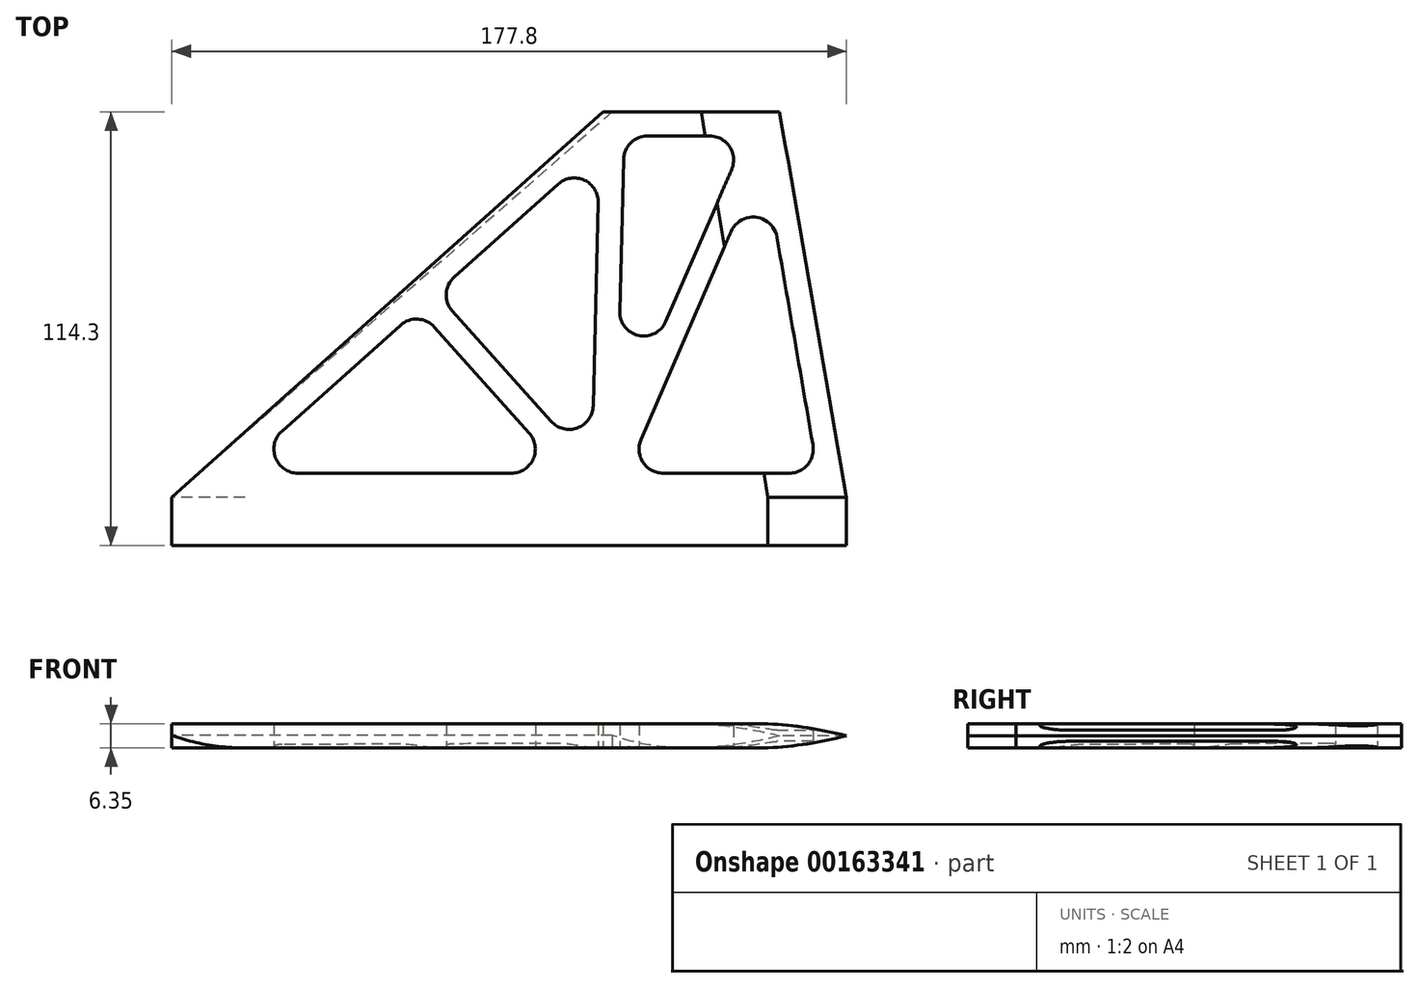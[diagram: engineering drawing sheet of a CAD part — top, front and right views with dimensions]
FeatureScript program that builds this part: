
annotation { "Feature Type Name" : "Feature", "Feature Type Description" : "" }
export const myFeature = defineFeature(function(context is Context, id is Id, definition is map)
    precondition{}
    {
        {
            var Q0;
            Q0=qCreatedBy(makeId("Top.planeOp"),FACE);
            var sketch = newSketch(context, id + "F0", { "sketchPlane" : qUnion([Q0])});
            skLineSegment(sketch, "E0", {"start": v(0, 0) * mm, "end": v(177.8, 0) * mm});
            skLineSegment(sketch, "E1", {"start": v(0, 0) * mm, "end": v(113.6, 101.6) * mm});
            skLineSegment(sketch, "E2", {"start": v(113.6, 101.6) * mm, "end": v(160.17, 101.6) * mm});
            skLineSegment(sketch, "E3", {"start": v(160.17, 101.6) * mm, "end": v(177.8, 0) * mm});
            skLineSegment(sketch, "E4.0", {"start": v(33.25, 6.35) * mm, "end": v(89.45, 6.35) * mm});
            skLineSegment(sketch, "E4.1", {"start": v(29.02, 17.43) * mm, "end": v(60.24, 45.36) * mm});
            skLineSegment(sketch, "E4.2", {"start": v(125.38, 95.25) * mm, "end": v(141.7, 95.25) * mm});
            skLineSegment(sketch, "E4.3", {"start": v(159.45, 68.6) * mm, "end": v(168.96, 13.79) * mm});
            skLineSegment(sketch, "E5.0", {"start": v(99.95, 20.02) * mm, "end": v(73.94, 49.1) * mm});
            skLineSegment(sketch, "E6.0", {"start": v(94.19, 16.93) * mm, "end": v(69.2, 44.86) * mm});
            skLineSegment(sketch, "E7.0", {"start": v(116.93, 6.27) * mm, "end": v(116.93, 6.35) * mm});
            skLineSegment(sketch, "E8.0", {"start": v(111.03, 24.09) * mm, "end": v(112.4, 77.65) * mm});
            skLineSegment(sketch, "E9.0", {"start": v(123.64, 15.22) * mm, "end": v(147.37, 70.03) * mm});
            skLineSegment(sketch, "E10.trimOffspring", {"start": v(118.02, 49.02) * mm, "end": v(119.04, 89.06) * mm});
            skLineSegment(sketch, "E11.trimOffspring", {"start": v(130.2, 46.34) * mm, "end": v(147.52, 86.38) * mm});
            skLineSegment(sketch, "E12.trimOffspring", {"start": v(129.47, 6.35) * mm, "end": v(162.7, 6.35) * mm});
            skLineSegment(sketch, "E13.trimOffspring", {"start": v(74.44, 58.06) * mm, "end": v(101.81, 82.54) * mm});
            skPoint(sketch, "E14.visualSharp", {"position": v(64.97, 49.6) * mm});
            skArc(sketch, "E14.filletArc", {"start": v(69.2, 44.86) * mm, "mid": v(64.83, 46.97) * mm, "end": v(60.24, 45.36) * mm});
            skPoint(sketch, "E15.visualSharp", {"position": v(69.7, 53.83) * mm});
            skArc(sketch, "E15.filletArc", {"start": v(74.44, 58.06) * mm, "mid": v(72.33, 53.68) * mm, "end": v(73.94, 49.1) * mm});
            skPoint(sketch, "E16.visualSharp", {"position": v(112.77, 92.34) * mm});
            skArc(sketch, "E16.filletArc", {"start": v(112.4, 77.65) * mm, "mid": v(108.71, 83.57) * mm, "end": v(101.81, 82.54) * mm});
            skPoint(sketch, "E17.visualSharp", {"position": v(119.2, 95.25) * mm});
            skArc(sketch, "E17.filletArc", {"start": v(125.38, 95.25) * mm, "mid": v(120.95, 93.45) * mm, "end": v(119.04, 89.06) * mm});
            skPoint(sketch, "E18.visualSharp", {"position": v(151.36, 95.25) * mm});
            skArc(sketch, "E18.filletArc", {"start": v(147.52, 86.38) * mm, "mid": v(147, 92.39) * mm, "end": v(141.7, 95.25) * mm});
            skPoint(sketch, "E19.visualSharp", {"position": v(155.81, 89.54) * mm});
            skArc(sketch, "E19.filletArc", {"start": v(159.45, 68.6) * mm, "mid": v(153.94, 73.81) * mm, "end": v(147.37, 70.03) * mm});
            skPoint(sketch, "E20.visualSharp", {"position": v(117.18, 16.29) * mm});
            skArc(sketch, "E20.filletArc", {"start": v(118.02, 49.02) * mm, "mid": v(123, 42.66) * mm, "end": v(130.2, 46.34) * mm});
            skPoint(sketch, "E21.visualSharp", {"position": v(110.62, 8.08) * mm});
            skArc(sketch, "E21.filletArc", {"start": v(99.95, 20.02) * mm, "mid": v(106.87, 18.29) * mm, "end": v(111.03, 24.09) * mm});
            skPoint(sketch, "E22.visualSharp", {"position": v(103.65, 6.35) * mm});
            skArc(sketch, "E22.filletArc", {"start": v(89.45, 6.35) * mm, "mid": v(95.25, 10.1) * mm, "end": v(94.19, 16.93) * mm});
            skPoint(sketch, "E23.visualSharp", {"position": v(16.62, 6.35) * mm});
            skArc(sketch, "E23.filletArc", {"start": v(29.02, 17.43) * mm, "mid": v(27.32, 10.43) * mm, "end": v(33.25, 6.35) * mm});
            skPoint(sketch, "E24.visualSharp", {"position": v(119.8, 6.35) * mm});
            skArc(sketch, "E24.filletArc", {"start": v(123.64, 15.22) * mm, "mid": v(124.16, 9.21) * mm, "end": v(129.47, 6.35) * mm});
            skPoint(sketch, "E25.visualSharp", {"position": v(170.25, 6.35) * mm});
            skArc(sketch, "E25.filletArc", {"start": v(162.7, 6.35) * mm, "mid": v(167.56, 8.61) * mm, "end": v(168.96, 13.79) * mm});
            skSolve(sketch);
        }
        {
            var Q0;
            Q0=makeQuery(id+"F0.imprint","IMPRINT",FACE,{"disambiguationData":[TD([[makeQuery(id+"F0.imprint","IMPRINT",EDGE,{"derivedFrom":sQuery(id+"F0.wireOp",EDGE,"E0")}),1.0]])]});
            extrude(context, id + "F1", {"entities" : qUnion([Q0]), "depth" : 6.35 * mm});
        }
        {
            var Q0;
            Q0=makeQuery(id+"F1.opExtrude","SWEPT_EDGE",EDGE,{"disambiguationData":[OSD([sQuery(id+"F0.wireOp",EDGE,"E0"),sQuery(id+"F0.wireOp",EDGE,"E1")])]});
            cPlane(context, id + "F2", {"entities" : qUnion([Q0]), "cplaneType" : CPlaneType.LINE_ANGLE, "offset" : 25.4 * mm, "angle" : 138.8 * degree, "width" : 152.4 * mm, "height" : 152.4 * mm});
        }
        {
            var Q0;
            Q0=qCreatedBy(id+"F2.planeOp",FACE);
            var sketch = newSketch(context, id + "F3", { "sketchPlane" : qUnion([Q0])});
            skLineSegment(sketch, "E26", {"start": v(0, 0) * mm, "end": v(0, 3.3) * mm});
            skLineSegment(sketch, "E27", {"start": v(0, 3.3) * mm, "end": v(-12.7, 3.3) * mm});
            skLineSegment(sketch, "E28", {"start": v(-12.7, 3.3) * mm, "end": v(-12.7, 0) * mm});
            skLineSegment(sketch, "E29", {"start": v(-12.7, 0) * mm, "end": v(0, 0) * mm});
            skArc(sketch, "E30", {"start": v(-12.7, 0) * mm, "mid": v(-6.14, 0.84) * mm, "end": v(0, 3.3) * mm});
            skArc(sketch, "E31.MirrorCS", {"start": v(-12.7, 6.6) * mm, "mid": v(-6.14, 5.77) * mm, "end": v(0, 3.3) * mm});
            skLineSegment(sketch, "E32", {"start": v(0, 3.3) * mm, "end": v(0, 6.6) * mm});
            skLineSegment(sketch, "E33", {"start": v(0, 6.6) * mm, "end": v(-12.7, 6.6) * mm});
            skSolve(sketch);
        }
        {
            var Q0;
            Q0=makeQuery(id+"F3.imprint","IMPRINT",FACE,{"disambiguationData":[TD([[makeQuery(id+"F3.imprint","IMPRINT",EDGE,{"derivedFrom":sQuery(id+"F3.wireOp",EDGE,"E31.MirrorCS")}),1.0]])]});
            var Q1;
            Q1=makeQuery(id+"F3.imprint","IMPRINT",FACE,{"disambiguationData":[TD([[makeQuery(id+"F3.imprint","IMPRINT",EDGE,{"derivedFrom":sQuery(id+"F3.wireOp",EDGE,"E26")}),1.0]])]});
            extrude(context, id + "F4", {"entities" : qUnion([Q0, Q1]), "operationType" : NewBodyOperationType.REMOVE, "depth" : 254 * mm});
        }
        {
            var Q0;
            Q0=makeQuery(id+"F1.opExtrude","SWEPT_EDGE",EDGE,{"disambiguationData":[OSD([sQuery(id+"F0.wireOp",EDGE,"E0"),sQuery(id+"F0.wireOp",EDGE,"E3")])]});
            cPlane(context, id + "F5", {"entities" : qUnion([Q0]), "cplaneType" : CPlaneType.LINE_ANGLE, "offset" : 25.4 * mm, "angle" : 260.15 * degree, "width" : 152.4 * mm, "height" : 152.4 * mm});
        }
        {
            var Q0;
            Q0=qCreatedBy(id+"F5.planeOp",FACE);
            var sketch = newSketch(context, id + "F6", { "sketchPlane" : qUnion([Q0])});
            skLineSegment(sketch, "E34", {"start": v(175.18, -0.13) * mm, "end": v(175.18, 3.18) * mm});
            skLineSegment(sketch, "E35", {"start": v(175.18, 3.18) * mm, "end": v(175.18, 6.48) * mm});
            skLineSegment(sketch, "E36", {"start": v(175.18, 3.18) * mm, "end": v(149.78, 3.18) * mm});
            skLineSegment(sketch, "E37", {"start": v(149.78, 3.18) * mm, "end": v(149.78, -0.13) * mm});
            skLineSegment(sketch, "E38", {"start": v(149.78, 3.18) * mm, "end": v(149.78, 6.48) * mm});
            skLineSegment(sketch, "E39", {"start": v(149.78, -0.13) * mm, "end": v(175.18, -0.13) * mm});
            skLineSegment(sketch, "E40", {"start": v(149.78, 6.48) * mm, "end": v(175.18, 6.48) * mm});
            skArc(sketch, "E41", {"start": v(149.78, -0.13) * mm, "mid": v(162.59, 0.7) * mm, "end": v(175.18, 3.17) * mm});
            skArc(sketch, "E42.MirrorCS", {"start": v(149.78, 6.48) * mm, "mid": v(162.59, 5.65) * mm, "end": v(175.18, 3.18) * mm});
            skSolve(sketch);
        }
        {
            var Q0;
            Q0=makeQuery(id+"F6.imprint","IMPRINT",FACE,{"disambiguationData":[TD([[makeQuery(id+"F6.imprint","IMPRINT",EDGE,{"derivedFrom":sQuery(id+"F6.wireOp",EDGE,"E35")}),1.0]])]});
            var Q1;
            Q1=makeQuery(id+"F6.imprint","IMPRINT",FACE,{"disambiguationData":[TD([[makeQuery(id+"F6.imprint","IMPRINT",EDGE,{"derivedFrom":sQuery(id+"F6.wireOp",EDGE,"E34")}),1.0]])]});
            extrude(context, id + "F7", {"entities" : qUnion([Q0, Q1]), "operationType" : NewBodyOperationType.REMOVE, "oppositeDirection" : true, "depth" : 254 * mm});
        }
        {
            var Q0;
            Q0=makeQuery(id+"F1.opExtrude","SWEPT_FACE",FACE,{"disambiguationData":[OSD([sQuery(id+"F0.wireOp",EDGE,"E0")])]});
            extrude(context, id + "F8", {"entities" : qUnion([Q0]), "operationType" : NewBodyOperationType.ADD, "depth" : 12.7 * mm});
        }
    });
